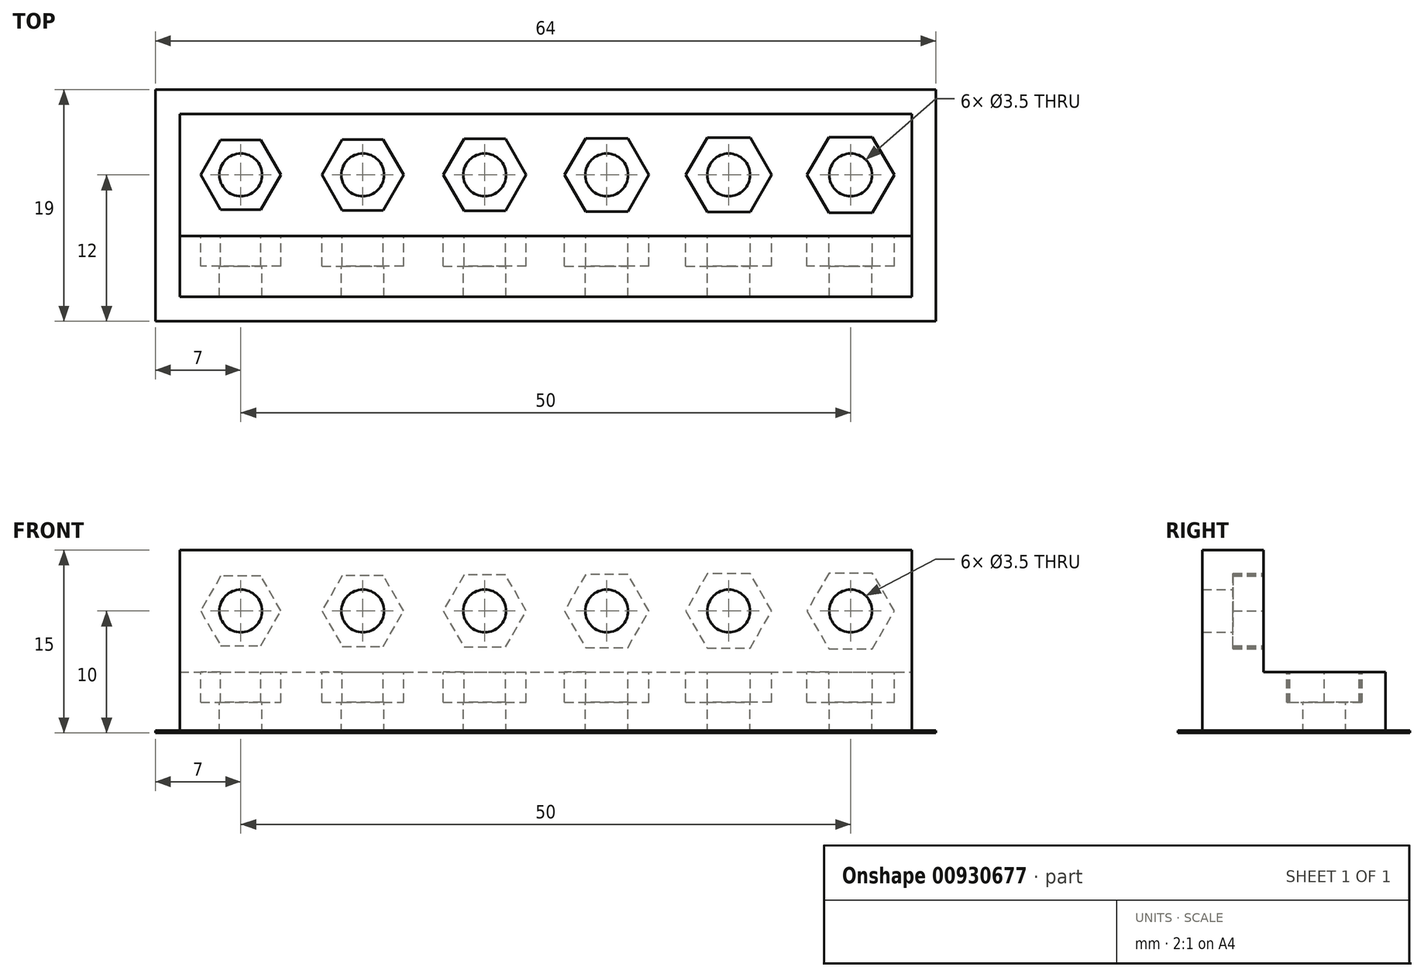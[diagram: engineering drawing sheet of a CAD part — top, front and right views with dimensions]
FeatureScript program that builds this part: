
annotation { "Feature Type Name" : "Feature", "Feature Type Description" : "" }
export const myFeature = defineFeature(function(context is Context, id is Id, definition is map)
    precondition{}
    {
        {
            var Q0;
            Q0=qCreatedBy(makeId("Top.planeOp"),FACE);
            var sketch = newSketch(context, id + "F0", { "sketchPlane" : qUnion([Q0])});
            skLineSegment(sketch, "E0.bottom", {"start": v(0, 0) * mm, "end": v(60, 0) * mm});
            skLineSegment(sketch, "E0.top", {"start": v(0, 15) * mm, "end": v(60, 15) * mm});
            skLineSegment(sketch, "E0.left", {"start": v(0, 0) * mm, "end": v(0, 15) * mm});
            skLineSegment(sketch, "E0.right", {"start": v(60, 0) * mm, "end": v(60, 15) * mm});
            skSolve(sketch);
        }
        {
            var Q0;
            Q0=qSketchRegion(id+"F0",true);
            extrude(context, id + "F1", {"entities" : qUnion([Q0]), "depth" : 5 * mm, "offsetDistance" : 25 * mm});
        }
        {
            var Q0;
            Q0=makeQuery(id+"F1.opExtrude","CAP_FACE",FACE,{"disambiguationData":[OSD([sQuery(id+"F0.wireOp",EDGE,"E0.bottom"),sQuery(id+"F0.wireOp",EDGE,"E0.top"),sQuery(id+"F0.wireOp",EDGE,"E0.left"),sQuery(id+"F0.wireOp",EDGE,"E0.right")])],"isStart":false});
            var sketch = newSketch(context, id + "F2", { "sketchPlane" : qUnion([Q0])});
            skLineSegment(sketch, "E1.bottom", {"start": v(0, 0) * mm, "end": v(60, 0) * mm});
            skLineSegment(sketch, "E1.top", {"start": v(0, 5) * mm, "end": v(60, 5) * mm});
            skLineSegment(sketch, "E1.left", {"start": v(0, 0) * mm, "end": v(0, 5) * mm});
            skLineSegment(sketch, "E1.right", {"start": v(60, 0) * mm, "end": v(60, 5) * mm});
            skSolve(sketch);
        }
        {
            var Q0;
            Q0=qSketchRegion(id+"F2",true);
            extrude(context, id + "F3", {"entities" : qUnion([Q0]), "operationType" : NewBodyOperationType.ADD, "depth" : 10 * mm, "offsetDistance" : 25 * mm});
        }
        {
            var Q0;
            Q0=makeQuery(id+"F1.opExtrude","CAP_FACE",FACE,{"disambiguationData":[OSD([sQuery(id+"F0.wireOp",EDGE,"E0.bottom"),sQuery(id+"F0.wireOp",EDGE,"E0.top"),sQuery(id+"F0.wireOp",EDGE,"E0.left"),sQuery(id+"F0.wireOp",EDGE,"E0.right")])],"isStart":false});
            var sketch = newSketch(context, id + "F4", { "sketchPlane" : qUnion([Q0])});
            skLineSegment(sketch, "E2", {"start": v(0, 10) * mm, "end": v(60, 10) * mm, "construction": true});
            skLineSegment(sketch, "E3", {"start": v(5, 15) * mm, "end": v(5, 5) * mm, "construction": true});
            skLineSegment(sketch, "E4", {"start": v(15, 15) * mm, "end": v(15, 5) * mm, "construction": true});
            skLineSegment(sketch, "E5", {"start": v(25, 15) * mm, "end": v(25, 5) * mm, "construction": true});
            skLineSegment(sketch, "E6", {"start": v(35, 15) * mm, "end": v(35, 5) * mm, "construction": true});
            skLineSegment(sketch, "E7", {"start": v(45, 15) * mm, "end": v(45, 5) * mm, "construction": true});
            skLineSegment(sketch, "E8", {"start": v(55, 15) * mm, "end": v(55, 5) * mm, "construction": true});
            skCircle(sketch, "E9.cCircle", {"center": v(5, 10) * mm, "radius": 2.85 * mm, "construction": true});
            skLineSegment(sketch, "E9.0", {"start": v(6.65, 12.85) * mm, "end": v(8.3, 10) * mm});
            skLineSegment(sketch, "E9.1", {"start": v(8.3, 10) * mm, "end": v(6.65, 7.15) * mm});
            skLineSegment(sketch, "E9.2", {"start": v(6.65, 7.15) * mm, "end": v(3.35, 7.15) * mm});
            skLineSegment(sketch, "E9.3", {"start": v(3.35, 7.15) * mm, "end": v(1.7, 10) * mm});
            skLineSegment(sketch, "E9.4", {"start": v(1.7, 10) * mm, "end": v(3.35, 12.85) * mm});
            skLineSegment(sketch, "E9.5", {"start": v(3.35, 12.85) * mm, "end": v(6.65, 12.85) * mm});
            skPoint(sketch, "E9.0.midPoint", {"position": v(7.47, 11.43) * mm});
            skCircle(sketch, "E10.cCircle", {"center": v(15, 10) * mm, "radius": 2.9 * mm, "construction": true});
            skLineSegment(sketch, "E10.0", {"start": v(16.67, 12.9) * mm, "end": v(18.35, 10) * mm});
            skLineSegment(sketch, "E10.1", {"start": v(18.35, 10) * mm, "end": v(16.67, 7.1) * mm});
            skLineSegment(sketch, "E10.2", {"start": v(16.67, 7.1) * mm, "end": v(13.33, 7.1) * mm});
            skLineSegment(sketch, "E10.3", {"start": v(13.33, 7.1) * mm, "end": v(11.65, 10) * mm});
            skLineSegment(sketch, "E10.4", {"start": v(11.65, 10) * mm, "end": v(13.33, 12.9) * mm});
            skLineSegment(sketch, "E10.5", {"start": v(13.33, 12.9) * mm, "end": v(16.67, 12.9) * mm});
            skPoint(sketch, "E10.0.midPoint", {"position": v(17.51, 11.45) * mm});
            skCircle(sketch, "E11.cCircle", {"center": v(25, 10) * mm, "radius": 2.95 * mm, "construction": true});
            skLineSegment(sketch, "E11.0", {"start": v(26.7, 12.95) * mm, "end": v(28.4, 10) * mm});
            skLineSegment(sketch, "E11.1", {"start": v(28.4, 10) * mm, "end": v(26.7, 7.05) * mm});
            skLineSegment(sketch, "E11.2", {"start": v(26.7, 7.05) * mm, "end": v(23.3, 7.05) * mm});
            skLineSegment(sketch, "E11.3", {"start": v(23.3, 7.05) * mm, "end": v(21.6, 10) * mm});
            skLineSegment(sketch, "E11.4", {"start": v(21.6, 10) * mm, "end": v(23.3, 12.95) * mm});
            skLineSegment(sketch, "E11.5", {"start": v(23.3, 12.95) * mm, "end": v(26.7, 12.95) * mm});
            skPoint(sketch, "E11.0.midPoint", {"position": v(27.55, 11.48) * mm});
            skCircle(sketch, "E12.cCircle", {"center": v(35, 10) * mm, "radius": 3 * mm, "construction": true});
            skLineSegment(sketch, "E12.0", {"start": v(36.73, 13) * mm, "end": v(38.46, 10) * mm});
            skLineSegment(sketch, "E12.1", {"start": v(38.46, 10) * mm, "end": v(36.73, 7) * mm});
            skLineSegment(sketch, "E12.2", {"start": v(36.73, 7) * mm, "end": v(33.27, 7) * mm});
            skLineSegment(sketch, "E12.3", {"start": v(33.27, 7) * mm, "end": v(31.54, 10) * mm});
            skLineSegment(sketch, "E12.4", {"start": v(31.54, 10) * mm, "end": v(33.27, 13) * mm});
            skLineSegment(sketch, "E12.5", {"start": v(33.27, 13) * mm, "end": v(36.73, 13) * mm});
            skPoint(sketch, "E12.0.midPoint", {"position": v(37.6, 11.5) * mm});
            skCircle(sketch, "E13.cCircle", {"center": v(45, 10) * mm, "radius": 3.05 * mm, "construction": true});
            skLineSegment(sketch, "E13.0", {"start": v(43.24, 13.05) * mm, "end": v(46.76, 13.05) * mm});
            skLineSegment(sketch, "E13.1", {"start": v(46.76, 13.05) * mm, "end": v(48.52, 10) * mm});
            skLineSegment(sketch, "E13.2", {"start": v(48.52, 10) * mm, "end": v(46.76, 6.95) * mm});
            skLineSegment(sketch, "E13.3", {"start": v(46.76, 6.95) * mm, "end": v(43.24, 6.95) * mm});
            skLineSegment(sketch, "E13.4", {"start": v(43.24, 6.95) * mm, "end": v(41.48, 10) * mm});
            skLineSegment(sketch, "E13.5", {"start": v(41.48, 10) * mm, "end": v(43.24, 13.05) * mm});
            skPoint(sketch, "E13.0.midPoint", {"position": v(45, 13.05) * mm});
            skCircle(sketch, "E14.cCircle", {"center": v(55, 10) * mm, "radius": 3.1 * mm, "construction": true});
            skLineSegment(sketch, "E14.0", {"start": v(56.79, 13.1) * mm, "end": v(58.58, 10) * mm});
            skLineSegment(sketch, "E14.1", {"start": v(58.58, 10) * mm, "end": v(56.79, 6.9) * mm});
            skLineSegment(sketch, "E14.2", {"start": v(56.79, 6.9) * mm, "end": v(53.21, 6.9) * mm});
            skLineSegment(sketch, "E14.3", {"start": v(53.21, 6.9) * mm, "end": v(51.42, 10) * mm});
            skLineSegment(sketch, "E14.4", {"start": v(51.42, 10) * mm, "end": v(53.21, 13.1) * mm});
            skLineSegment(sketch, "E14.5", {"start": v(53.21, 13.1) * mm, "end": v(56.79, 13.1) * mm});
            skPoint(sketch, "E14.0.midPoint", {"position": v(57.68, 11.55) * mm});
            skSolve(sketch);
        }
        {
            var Q0;
            Q0=qSketchRegion(id+"F4",true);
            extrude(context, id + "F5", {"entities" : qUnion([Q0]), "operationType" : NewBodyOperationType.REMOVE, "oppositeDirection" : true, "depth" : 2.5 * mm, "offsetDistance" : 25 * mm});
        }
        {
            var Q0;
            Q0=makeQuery(id+"F5.boolean.opBoolean","COPY",FACE,{"derivedFrom":makeQuery(id+"F5.opExtrude","CAP_FACE",FACE,{"disambiguationData":[OSD([sQuery(id+"F4.wireOp",EDGE,"E9.0"),sQuery(id+"F4.wireOp",EDGE,"E9.1"),sQuery(id+"F4.wireOp",EDGE,"E9.2"),sQuery(id+"F4.wireOp",EDGE,"E9.3"),sQuery(id+"F4.wireOp",EDGE,"E9.4"),sQuery(id+"F4.wireOp",EDGE,"E9.5")])],"isStart":false})});
            var sketch = newSketch(context, id + "F6", { "sketchPlane" : qUnion([Q0])});
            skCircle(sketch, "E15", {"center": v(5, 10) * mm, "radius": 1.75 * mm});
            skCircle(sketch, "E16", {"center": v(15, 10) * mm, "radius": 1.75 * mm});
            skCircle(sketch, "E17", {"center": v(25, 10) * mm, "radius": 1.75 * mm});
            skCircle(sketch, "E18", {"center": v(35, 10) * mm, "radius": 1.75 * mm});
            skCircle(sketch, "E19", {"center": v(45, 10) * mm, "radius": 1.75 * mm});
            skCircle(sketch, "E20", {"center": v(55, 10) * mm, "radius": 1.75 * mm});
            skLineSegment(sketch, "E21", {"start": v(3.35, 12.85) * mm, "end": v(5, 10) * mm, "construction": true});
            skLineSegment(sketch, "E22", {"start": v(5, 10) * mm, "end": v(6.65, 12.85) * mm, "construction": true});
            skLineSegment(sketch, "E23", {"start": v(15, 10) * mm, "end": v(16.67, 12.9) * mm, "construction": true});
            skLineSegment(sketch, "E24", {"start": v(15, 10) * mm, "end": v(13.33, 12.9) * mm, "construction": true});
            skLineSegment(sketch, "E25", {"start": v(23.3, 12.95) * mm, "end": v(25, 10) * mm, "construction": true});
            skLineSegment(sketch, "E26", {"start": v(25, 10) * mm, "end": v(26.7, 12.95) * mm, "construction": true});
            skLineSegment(sketch, "E27", {"start": v(33.27, 13) * mm, "end": v(35, 10) * mm, "construction": true});
            skLineSegment(sketch, "E28", {"start": v(35, 10) * mm, "end": v(36.73, 13) * mm, "construction": true});
            skLineSegment(sketch, "E29", {"start": v(43.24, 13.05) * mm, "end": v(45, 10) * mm, "construction": true});
            skLineSegment(sketch, "E30", {"start": v(45, 10) * mm, "end": v(46.76, 13.05) * mm, "construction": true});
            skLineSegment(sketch, "E31", {"start": v(53.21, 13.1) * mm, "end": v(55, 10) * mm, "construction": true});
            skLineSegment(sketch, "E32", {"start": v(55, 10) * mm, "end": v(56.79, 13.1) * mm, "construction": true});
            skSolve(sketch);
        }
        {
            var Q0;
            Q0=qSketchRegion(id+"F6",true);
            extrude(context, id + "F7", {"entities" : qUnion([Q0]), "operationType" : NewBodyOperationType.REMOVE, "endBound" : BoundingType.UP_TO_NEXT, "oppositeDirection" : true, "depth" : 25 * mm, "offsetDistance" : 25 * mm});
        }
        {
            var Q0;
            Q0=makeQuery(id+"F3.opExtrude","SWEPT_FACE",FACE,{"disambiguationData":[OSD([sQuery(id+"F2.wireOp",EDGE,"E1.top")])]});
            var sketch = newSketch(context, id + "F8", { "sketchPlane" : qUnion([Q0])});
            skLineSegment(sketch, "E33", {"start": v(-60, 10) * mm, "end": v(0, 10) * mm, "construction": true});
            skLineSegment(sketch, "E34", {"start": v(-55, 15) * mm, "end": v(-55, 5) * mm, "construction": true});
            skLineSegment(sketch, "E35", {"start": v(-45, 15) * mm, "end": v(-45, 5) * mm, "construction": true});
            skLineSegment(sketch, "E36", {"start": v(-35, 15) * mm, "end": v(-35, 5) * mm, "construction": true});
            skLineSegment(sketch, "E37", {"start": v(-25, 15) * mm, "end": v(-25, 5) * mm, "construction": true});
            skLineSegment(sketch, "E38", {"start": v(-15, 15) * mm, "end": v(-15, 5) * mm, "construction": true});
            skLineSegment(sketch, "E39", {"start": v(-5, 15) * mm, "end": v(-5, 5) * mm, "construction": true});
            skCircle(sketch, "E40.cCircle", {"center": v(-55, 10) * mm, "radius": 3.1 * mm, "construction": true});
            skLineSegment(sketch, "E40.0", {"start": v(-53.21, 13.1) * mm, "end": v(-51.42, 10) * mm});
            skLineSegment(sketch, "E40.1", {"start": v(-51.42, 10) * mm, "end": v(-53.21, 6.9) * mm});
            skLineSegment(sketch, "E40.2", {"start": v(-53.21, 6.9) * mm, "end": v(-56.79, 6.9) * mm});
            skLineSegment(sketch, "E40.3", {"start": v(-56.79, 6.9) * mm, "end": v(-58.58, 10) * mm});
            skLineSegment(sketch, "E40.4", {"start": v(-58.58, 10) * mm, "end": v(-56.79, 13.1) * mm});
            skLineSegment(sketch, "E40.5", {"start": v(-56.79, 13.1) * mm, "end": v(-53.21, 13.1) * mm});
            skPoint(sketch, "E40.0.midPoint", {"position": v(-52.32, 11.55) * mm});
            skCircle(sketch, "E41.cCircle", {"center": v(-45, 10) * mm, "radius": 3.05 * mm, "construction": true});
            skLineSegment(sketch, "E41.0", {"start": v(-46.76, 13.05) * mm, "end": v(-43.24, 13.05) * mm});
            skLineSegment(sketch, "E41.1", {"start": v(-43.24, 13.05) * mm, "end": v(-41.48, 10) * mm});
            skLineSegment(sketch, "E41.2", {"start": v(-41.48, 10) * mm, "end": v(-43.24, 6.95) * mm});
            skLineSegment(sketch, "E41.3", {"start": v(-43.24, 6.95) * mm, "end": v(-46.76, 6.95) * mm});
            skLineSegment(sketch, "E41.4", {"start": v(-46.76, 6.95) * mm, "end": v(-48.52, 10) * mm});
            skLineSegment(sketch, "E41.5", {"start": v(-48.52, 10) * mm, "end": v(-46.76, 13.05) * mm});
            skPoint(sketch, "E41.0.midPoint", {"position": v(-45, 13.05) * mm});
            skCircle(sketch, "E42.cCircle", {"center": v(-35, 10) * mm, "radius": 3 * mm, "construction": true});
            skLineSegment(sketch, "E42.0", {"start": v(-36.73, 13) * mm, "end": v(-33.27, 13) * mm});
            skLineSegment(sketch, "E42.1", {"start": v(-33.27, 13) * mm, "end": v(-31.54, 10) * mm});
            skLineSegment(sketch, "E42.2", {"start": v(-31.54, 10) * mm, "end": v(-33.27, 7) * mm});
            skLineSegment(sketch, "E42.3", {"start": v(-33.27, 7) * mm, "end": v(-36.73, 7) * mm});
            skLineSegment(sketch, "E42.4", {"start": v(-36.73, 7) * mm, "end": v(-38.46, 10) * mm});
            skLineSegment(sketch, "E42.5", {"start": v(-38.46, 10) * mm, "end": v(-36.73, 13) * mm});
            skPoint(sketch, "E42.0.midPoint", {"position": v(-35, 13) * mm});
            skCircle(sketch, "E43.cCircle", {"center": v(-25, 10) * mm, "radius": 2.95 * mm, "construction": true});
            skLineSegment(sketch, "E43.0", {"start": v(-26.7, 12.95) * mm, "end": v(-23.3, 12.95) * mm});
            skLineSegment(sketch, "E43.1", {"start": v(-23.3, 12.95) * mm, "end": v(-21.6, 10) * mm});
            skLineSegment(sketch, "E43.2", {"start": v(-21.6, 10) * mm, "end": v(-23.3, 7.05) * mm});
            skLineSegment(sketch, "E43.3", {"start": v(-23.3, 7.05) * mm, "end": v(-26.7, 7.05) * mm});
            skLineSegment(sketch, "E43.4", {"start": v(-26.7, 7.05) * mm, "end": v(-28.4, 10) * mm});
            skLineSegment(sketch, "E43.5", {"start": v(-28.4, 10) * mm, "end": v(-26.7, 12.95) * mm});
            skPoint(sketch, "E43.0.midPoint", {"position": v(-25, 12.95) * mm});
            skCircle(sketch, "E44.cCircle", {"center": v(-15, 10) * mm, "radius": 2.9 * mm, "construction": true});
            skLineSegment(sketch, "E44.0", {"start": v(-16.67, 12.9) * mm, "end": v(-13.33, 12.9) * mm});
            skLineSegment(sketch, "E44.1", {"start": v(-13.33, 12.9) * mm, "end": v(-11.65, 10) * mm});
            skLineSegment(sketch, "E44.2", {"start": v(-11.65, 10) * mm, "end": v(-13.33, 7.1) * mm});
            skLineSegment(sketch, "E44.3", {"start": v(-13.33, 7.1) * mm, "end": v(-16.67, 7.1) * mm});
            skLineSegment(sketch, "E44.4", {"start": v(-16.67, 7.1) * mm, "end": v(-18.35, 10) * mm});
            skLineSegment(sketch, "E44.5", {"start": v(-18.35, 10) * mm, "end": v(-16.67, 12.9) * mm});
            skPoint(sketch, "E44.0.midPoint", {"position": v(-15, 12.9) * mm});
            skCircle(sketch, "E45.cCircle", {"center": v(-5, 10) * mm, "radius": 2.85 * mm, "construction": true});
            skLineSegment(sketch, "E45.0", {"start": v(-3.35, 12.85) * mm, "end": v(-1.7, 10) * mm});
            skLineSegment(sketch, "E45.1", {"start": v(-1.7, 10) * mm, "end": v(-3.35, 7.15) * mm});
            skLineSegment(sketch, "E45.2", {"start": v(-3.35, 7.15) * mm, "end": v(-6.65, 7.15) * mm});
            skLineSegment(sketch, "E45.3", {"start": v(-6.65, 7.15) * mm, "end": v(-8.3, 10) * mm});
            skLineSegment(sketch, "E45.4", {"start": v(-8.3, 10) * mm, "end": v(-6.65, 12.85) * mm});
            skLineSegment(sketch, "E45.5", {"start": v(-6.65, 12.85) * mm, "end": v(-3.35, 12.85) * mm});
            skPoint(sketch, "E45.0.midPoint", {"position": v(-2.53, 11.43) * mm});
            skSolve(sketch);
        }
        {
            var Q0;
            Q0=qSketchRegion(id+"F8",true);
            extrude(context, id + "F9", {"entities" : qUnion([Q0]), "operationType" : NewBodyOperationType.REMOVE, "oppositeDirection" : true, "depth" : 2.5 * mm, "offsetDistance" : 25 * mm});
        }
        {
            var Q0;
            Q0=makeQuery(id+"F9.boolean.opBoolean","COPY",FACE,{"derivedFrom":makeQuery(id+"F9.opExtrude","CAP_FACE",FACE,{"disambiguationData":[OSD([sQuery(id+"F8.wireOp",EDGE,"E40.0"),sQuery(id+"F8.wireOp",EDGE,"E40.1"),sQuery(id+"F8.wireOp",EDGE,"E40.2"),sQuery(id+"F8.wireOp",EDGE,"E40.3"),sQuery(id+"F8.wireOp",EDGE,"E40.4"),sQuery(id+"F8.wireOp",EDGE,"E40.5")])],"isStart":false})});
            var sketch = newSketch(context, id + "F10", { "sketchPlane" : qUnion([Q0])});
            skCircle(sketch, "E46", {"center": v(-55, 10) * mm, "radius": 1.75 * mm});
            skCircle(sketch, "E47", {"center": v(-45, 10) * mm, "radius": 1.75 * mm});
            skCircle(sketch, "E48", {"center": v(-35, 10) * mm, "radius": 1.75 * mm});
            skCircle(sketch, "E49", {"center": v(-25, 10) * mm, "radius": 1.75 * mm});
            skCircle(sketch, "E50", {"center": v(-15, 10) * mm, "radius": 1.75 * mm});
            skCircle(sketch, "E51", {"center": v(-5, 10) * mm, "radius": 1.75 * mm});
            skLineSegment(sketch, "E52", {"start": v(-56.79, 13.1) * mm, "end": v(-55, 10) * mm, "construction": true});
            skLineSegment(sketch, "E53", {"start": v(-55, 10) * mm, "end": v(-53.21, 13.1) * mm, "construction": true});
            skLineSegment(sketch, "E54", {"start": v(-46.76, 13.05) * mm, "end": v(-45, 10) * mm, "construction": true});
            skLineSegment(sketch, "E55", {"start": v(-45, 10) * mm, "end": v(-43.24, 13.05) * mm, "construction": true});
            skLineSegment(sketch, "E56", {"start": v(-36.73, 13) * mm, "end": v(-35, 10) * mm, "construction": true});
            skLineSegment(sketch, "E57", {"start": v(-33.27, 13) * mm, "end": v(-35, 10) * mm, "construction": true});
            skLineSegment(sketch, "E58", {"start": v(-25, 10) * mm, "end": v(-26.7, 12.95) * mm, "construction": true});
            skLineSegment(sketch, "E59", {"start": v(-25, 10) * mm, "end": v(-23.3, 12.95) * mm, "construction": true});
            skLineSegment(sketch, "E60", {"start": v(-16.67, 12.9) * mm, "end": v(-15, 10) * mm, "construction": true});
            skLineSegment(sketch, "E61", {"start": v(-15, 10) * mm, "end": v(-13.33, 12.9) * mm, "construction": true});
            skLineSegment(sketch, "E62", {"start": v(-6.65, 12.85) * mm, "end": v(-5, 10) * mm, "construction": true});
            skLineSegment(sketch, "E63", {"start": v(-3.35, 12.85) * mm, "end": v(-5, 10) * mm, "construction": true});
            skLineSegment(sketch, "E64", {"start": v(-58.58, 10) * mm, "end": v(-1.7, 10) * mm, "construction": true});
            skSolve(sketch);
        }
        {
            var Q0;
            Q0=qSketchRegion(id+"F10",true);
            extrude(context, id + "F11", {"entities" : qUnion([Q0]), "operationType" : NewBodyOperationType.REMOVE, "endBound" : BoundingType.UP_TO_NEXT, "oppositeDirection" : true, "depth" : 25 * mm, "offsetDistance" : 25 * mm});
        }
        {
            var Q0;
            Q0=qCreatedBy(makeId("Top.planeOp"),FACE);
            var sketch = newSketch(context, id + "F12", { "sketchPlane" : qUnion([Q0])});
            skLineSegment(sketch, "E65", {"start": v(0, 0) * mm, "end": v(0, 15) * mm});
            skLineSegment(sketch, "E66", {"start": v(0, 15) * mm, "end": v(60, 15) * mm});
            skLineSegment(sketch, "E67", {"start": v(60, 15) * mm, "end": v(60, 0) * mm});
            skLineSegment(sketch, "E68", {"start": v(60, 0) * mm, "end": v(0, 0) * mm});
            skLineSegment(sketch, "E69.bottom", {"start": v(-2, 17) * mm, "end": v(62, 17) * mm});
            skLineSegment(sketch, "E69.top", {"start": v(-2, -2) * mm, "end": v(62, -2) * mm});
            skLineSegment(sketch, "E69.left", {"start": v(-2, 17) * mm, "end": v(-2, -2) * mm});
            skLineSegment(sketch, "E69.right", {"start": v(62, 17) * mm, "end": v(62, -2) * mm});
            skSolve(sketch);
        }
        {
            var Q0;
            Q0=qSketchRegion(id+"F12",true);
            extrude(context, id + "F13", {"entities" : qUnion([Q0]), "operationType" : NewBodyOperationType.ADD, "depth" : 0.2 * mm, "offsetDistance" : 25 * mm});
        }
    });
